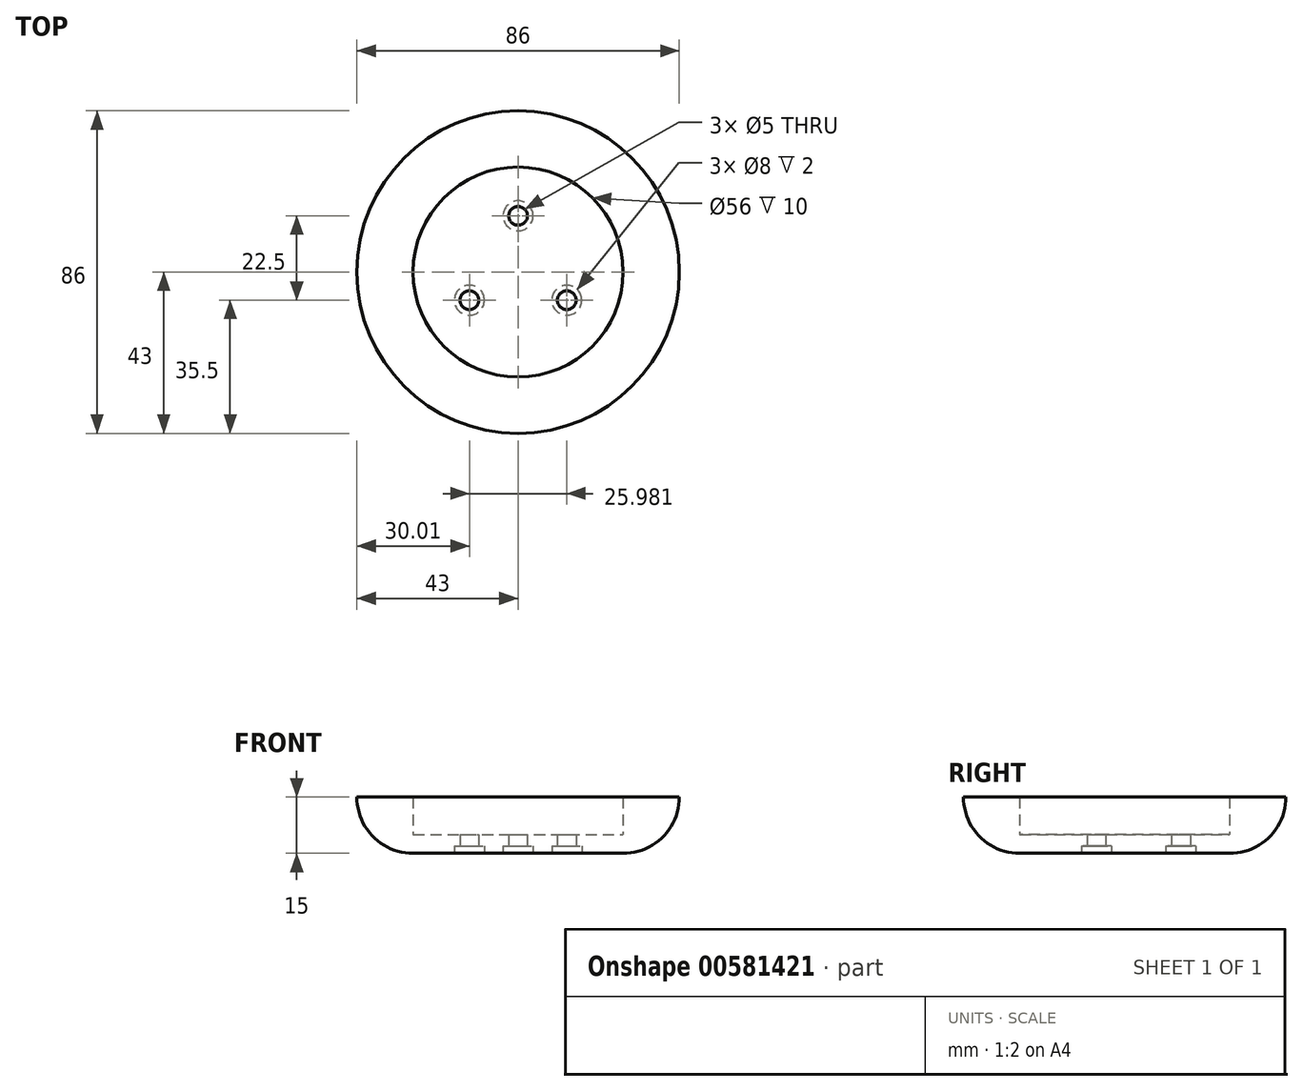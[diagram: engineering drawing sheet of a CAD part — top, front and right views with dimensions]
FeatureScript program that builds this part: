
annotation { "Feature Type Name" : "Feature", "Feature Type Description" : "" }
export const myFeature = defineFeature(function(context is Context, id is Id, definition is map)
    precondition{}
    {
        {
            var Q0;
            Q0=qCreatedBy(makeId("Front.planeOp"),FACE);
            var sketch = newSketch(context, id + "F0", { "sketchPlane" : qUnion([Q0])});
            skLineSegment(sketch, "E0", {"start": v(0, -25) * mm, "end": v(28, -25) * mm});
            skLineSegment(sketch, "E1", {"start": v(28, -25) * mm, "end": v(28, -15) * mm});
            skLineSegment(sketch, "E2", {"start": v(28, -15) * mm, "end": v(43, -15) * mm});
            skLineSegment(sketch, "E3", {"start": v(43, -15) * mm, "end": v(43, -30) * mm});
            skLineSegment(sketch, "E4", {"start": v(43, -30) * mm, "end": v(0, -30) * mm});
            skLineSegment(sketch, "E5", {"start": v(0, -30) * mm, "end": v(0, -25) * mm});
            skSolve(sketch);
        }
        {
            var Q0;
            Q0=makeQuery(id+"F0.imprint","IMPRINT",FACE,{"disambiguationData":[TD([[makeQuery(id+"F0.imprint","IMPRINT",EDGE,{"derivedFrom":sQuery(id+"F0.wireOp",EDGE,"E0")}),-1.0]])]});
            var Q1;
            Q1=sQuery(id+"F0.wireOp",EDGE,"E5");
            revolve(context, id + "F1", {"entities" : qUnion([Q0]), "axis" : qUnion([Q1]), "revolveType" : RevolveType.FULL});
        }
        {
            var Q0;
            Q0=makeQuery(id+"F1.opRevolve","SWEPT_EDGE",EDGE,{"disambiguationData":[OSD([sQuery(id+"F0.wireOp",EDGE,"E3"),sQuery(id+"F0.wireOp",EDGE,"E4")])]});
            fillet(context, id + "F2", {"entities" : qUnion([Q0]), "radius" : 15 * mm, "tangentPropagation" : true, "allowEdgeOverflow" : false});
        }
        {
            var Q0;
            Q0=makeQuery(id+"F1.opRevolve","SWEPT_FACE",FACE,{"disambiguationData":[OSD([sQuery(id+"F0.wireOp",EDGE,"E4")])]});
            var sketch = newSketch(context, id + "F3", { "sketchPlane" : qUnion([Q0])});
            skPoint(sketch, "E6.center", {"position": v(0, 0) * mm});
            skPoint(sketch, "E7", {"position": v(0, -15) * mm});
            skPoint(sketch, "E8.1.1", {"position": v(13, 7.5) * mm});
            skPoint(sketch, "E8.2.1", {"position": v(-13, 7.5) * mm});
            skSolve(sketch);
        }
        {
            var Q0;
            Q0=sQuery(id+"F3.wireOp",VERTEX,"E8.2.1");
            var Q1;
            Q1=sQuery(id+"F3.wireOp",VERTEX,"E8.1.1");
            var Q2;
            Q2=sQuery(id+"F3.wireOp",VERTEX,"E7");
            var Q3;
            Q3=makeQuery(id+"F1.opRevolve","SWEPT_BODY",BODY,{"disambiguationData":[OSD([sQuery(id+"F0.wireOp",EDGE,"E0"),sQuery(id+"F0.wireOp",EDGE,"E1"),sQuery(id+"F0.wireOp",EDGE,"E2"),sQuery(id+"F0.wireOp",EDGE,"E3"),sQuery(id+"F0.wireOp",EDGE,"E4"),sQuery(id+"F0.wireOp",EDGE,"E5")])]});
            hole(context, id + "F4", {"style" : HoleStyle.C_BORE, "endStyle" : HoleEndStyle.THROUGH, "holeDiameter" : 5 * mm, "cBoreDiameter" : 8 * mm, "cBoreDepth" : 2 * mm, "majorDiameter" : 5 * mm, "isTappedThrough" : true, "tappedDepth" : 12 * mm, "tapClearance" : 3, "locations" : qUnion([Q0, Q1, Q2]), "scope" : qUnion([Q3])});
        }
    });
